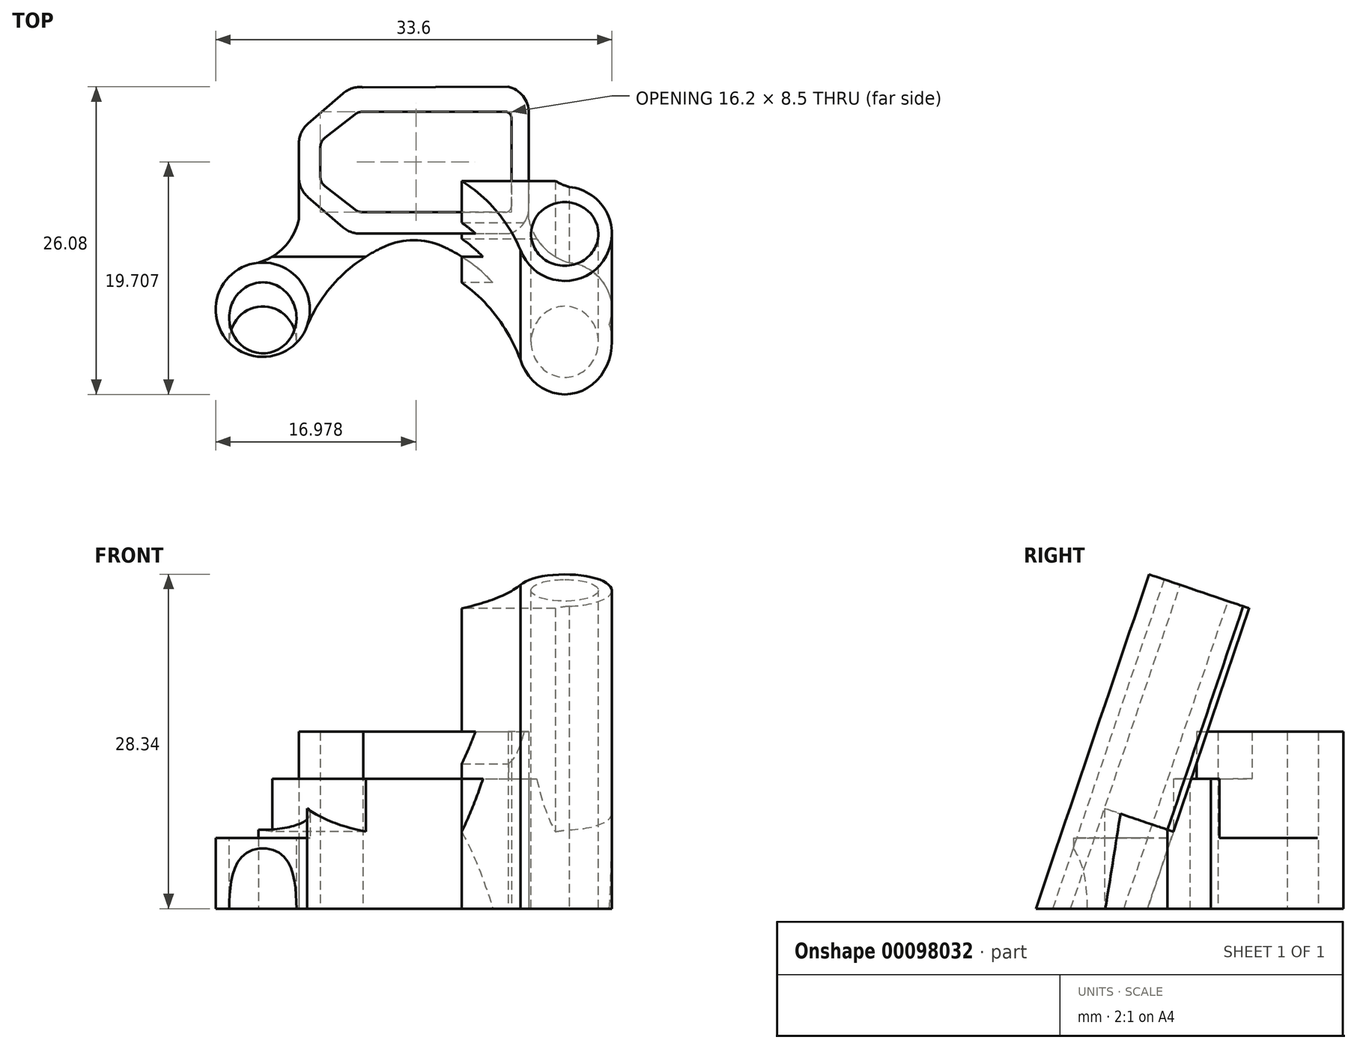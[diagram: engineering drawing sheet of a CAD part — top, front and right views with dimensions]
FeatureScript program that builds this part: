
annotation { "Feature Type Name" : "Feature", "Feature Type Description" : "" }
export const myFeature = defineFeature(function(context is Context, id is Id, definition is map)
    precondition{}
    {
        {
            var Q0;
            Q0=qCreatedBy(makeId("Top.planeOp"),FACE);
            var sketch = newSketch(context, id + "F0", { "sketchPlane" : qUnion([Q0])});
            skLineSegment(sketch, "E0", {"start": v(0.28, -14.51) * mm, "end": v(13.08, -14.51) * mm, "construction": true});
            skLineSegment(sketch, "E1", {"start": v(0.28, -14.51) * mm, "end": v(0.28, -2.01) * mm, "construction": true});
            skLineSegment(sketch, "E2.0", {"start": v(-4.02, 4.34) * mm, "end": v(8.28, 4.38) * mm});
            skLineSegment(sketch, "E3.0", {"start": v(-5.73, 3.81) * mm, "end": v(-8.7, 1.24) * mm});
            skLineSegment(sketch, "E4.0", {"start": v(10.02, -6.85) * mm, "end": v(10.02, 2.19) * mm});
            skLineSegment(sketch, "E5.MirrorCS", {"start": v(-9.47, -6.85) * mm, "end": v(-9.47, -0.37) * mm});
            skArc(sketch, "E6", {"start": v(-8.7, 1.24) * mm, "mid": v(-9.25, 0.52) * mm, "end": v(-9.47, -0.37) * mm});
            skPoint(sketch, "E7.orphan", {"position": v(-9.47, 2.19) * mm});
            skPoint(sketch, "E8.orphan", {"position": v(-9.47, -9.56) * mm});
            skArc(sketch, "E9", {"start": v(-4.02, 4.34) * mm, "mid": v(-4.93, 4.26) * mm, "end": v(-5.73, 3.81) * mm});
            skArc(sketch, "E10", {"start": v(10.02, 2.19) * mm, "mid": v(9.54, 3.6) * mm, "end": v(8.28, 4.38) * mm});
            skPoint(sketch, "E11.orphan", {"position": v(10.02, -9.56) * mm});
            skPoint(sketch, "E12.visualSharp", {"position": v(-11.2, -17.76) * mm});
            skArc(sketch, "E12.filletArc", {"start": v(-11.24, -17.77) * mm, "mid": v(-11.21, -17.75) * mm, "end": v(-11.2, -17.73) * mm});
            skArc(sketch, "E13", {"start": v(9.31, -15.87) * mm, "mid": v(16.24, -16.97) * mm, "end": v(13.46, -10.53) * mm});
            skArc(sketch, "E14", {"start": v(10.02, -6.85) * mm, "mid": v(11.23, -9.17) * mm, "end": v(13.46, -10.53) * mm});
            skArc(sketch, "E15.MirrorCS", {"start": v(-8.76, -15.87) * mm, "mid": v(-15.68, -16.97) * mm, "end": v(-12.9, -10.53) * mm});
            skArc(sketch, "E16.MirrorCS", {"start": v(-9.47, -6.85) * mm, "mid": v(-10.67, -9.17) * mm, "end": v(-12.9, -10.53) * mm});
            skPoint(sketch, "E17.orphan", {"position": v(2.83, -12.51) * mm});
            skPoint(sketch, "E18.0.start.orphan", {"position": v(-2.27, -12.51) * mm});
            skPoint(sketch, "E19.orphan", {"position": v(-1.11, -9.3) * mm});
            skPoint(sketch, "E20.center.orphan", {"position": v(0.28, -12.51) * mm});
            skPoint(sketch, "E20.start.orphan", {"position": v(1.67, -9.3) * mm});
            skCircle(sketch, "E21", {"center": v(0.28, -14.51) * mm, "radius": 5.89 * mm});
            skArc(sketch, "E22", {"start": v(-1.95, -9.06) * mm, "mid": v(-6.02, -11.8) * mm, "end": v(-8.76, -15.87) * mm});
            skArc(sketch, "E23.MirrorCS", {"start": v(2.5, -9.06) * mm, "mid": v(6.58, -11.8) * mm, "end": v(9.31, -15.87) * mm});
            skSolve(sketch);
        }
        {
            var Q0;
            Q0=makeQuery(id+"F0.imprint","IMPRINT",FACE,{"disambiguationData":[TD([[makeQuery(id+"F0.imprint","IMPRINT",EDGE,{"derivedFrom":sQuery(id+"F0.wireOp",EDGE,"d4629911-5982-4b6f-971a-48b49fc914d7")}),1.0]])]});
            var Q1;
            Q1=makeQuery(id+"F0.imprint","IMPRINT",FACE,{"disambiguationData":[TD([[makeQuery(id+"F0.imprint","IMPRINT",EDGE,{"derivedFrom":sQuery(id+"F0.wireOp",EDGE,"0au38lyi-hCIC-q0mX-iSc1-wrUDnvVJG4AV")}),-1.0]])]});
            var Q2;
            Q2=makeQuery(id+"F0.imprint","IMPRINT",FACE,{"disambiguationData":[TD([[makeQuery(id+"F0.imprint","IMPRINT",EDGE,{"derivedFrom":sQuery(id+"F0.wireOp",EDGE,"E2.0")}),-1.0]])]});
            extrude(context, id + "F1", {"entities" : qUnion([Q0, Q1, Q2]), "depth" : 6 * mm});
        }
        {
            var Q0;
            Q0=qCreatedBy(makeId("Top.planeOp"),FACE);
            var sketch = newSketch(context, id + "F2", { "sketchPlane" : qUnion([Q0])});
            skPoint(sketch, "E24.endSnap0", {"position": v(10, -2.09) * mm});
            skLineSegment(sketch, "E25", {"start": v(0.56, -2) * mm, "end": v(0.56, 2.26) * mm, "construction": true});
            skLineSegment(sketch, "E26", {"start": v(0.56, -2) * mm, "end": v(8.56, -2) * mm, "construction": true});
            skLineSegment(sketch, "E27", {"start": v(0.56, -2) * mm, "end": v(-7.64, -2) * mm, "construction": true});
            skLineSegment(sketch, "E28", {"start": v(8.56, 1.76) * mm, "end": v(8.56, -2) * mm});
            skLineSegment(sketch, "E29", {"start": v(8.06, 2.26) * mm, "end": v(-4.1, 2.26) * mm});
            skLineSegment(sketch, "E30", {"start": v(-7.64, -2) * mm, "end": v(-7.64, -0.73) * mm});
            skLineSegment(sketch, "E31", {"start": v(-7.26, 0.06) * mm, "end": v(-4.71, 2.04) * mm});
            skLineSegment(sketch, "E32.MirrorCS", {"start": v(8.06, -6.24) * mm, "end": v(-4.1, -6.24) * mm});
            skLineSegment(sketch, "E33.MirrorCS", {"start": v(-7.26, -4.04) * mm, "end": v(-4.71, -6.03) * mm});
            skLineSegment(sketch, "E34.MirrorCS", {"start": v(8.56, -5.74) * mm, "end": v(8.56, -2) * mm});
            skLineSegment(sketch, "E35.MirrorCS", {"start": v(-7.64, -2) * mm, "end": v(-7.64, -3.26) * mm});
            skPoint(sketch, "E36.visualSharp", {"position": v(-4.44, 2.26) * mm});
            skArc(sketch, "E36.filletArc", {"start": v(-4.1, 2.26) * mm, "mid": v(-4.42, 2.2) * mm, "end": v(-4.71, 2.04) * mm});
            skPoint(sketch, "E37.visualSharp", {"position": v(-4.44, -6.24) * mm});
            skArc(sketch, "E37.filletArc", {"start": v(-4.71, -6.03) * mm, "mid": v(-4.42, -6.19) * mm, "end": v(-4.1, -6.24) * mm});
            skPoint(sketch, "E38.visualSharp", {"position": v(8.56, -6.24) * mm});
            skArc(sketch, "E38.filletArc", {"start": v(8.06, -6.24) * mm, "mid": v(8.41, -6.1) * mm, "end": v(8.56, -5.74) * mm});
            skPoint(sketch, "E39.visualSharp", {"position": v(8.56, 2.26) * mm});
            skArc(sketch, "E39.filletArc", {"start": v(8.56, 1.76) * mm, "mid": v(8.41, 2.11) * mm, "end": v(8.06, 2.26) * mm});
            skPoint(sketch, "E40.visualSharp", {"position": v(-7.64, -0.24) * mm});
            skArc(sketch, "E40.filletArc", {"start": v(-7.26, 0.06) * mm, "mid": v(-7.54, -0.3) * mm, "end": v(-7.64, -0.73) * mm});
            skPoint(sketch, "E41.visualSharp", {"position": v(-7.64, -3.74) * mm});
            skArc(sketch, "E41.filletArc", {"start": v(-7.64, -3.26) * mm, "mid": v(-7.54, -3.7) * mm, "end": v(-7.26, -4.04) * mm});
            skSolve(sketch);
        }
        {
            var Q0;
            Q0=makeQuery(id+"F1.opExtrude","CAP_FACE",FACE,{"disambiguationData":[OSD([sQuery(id+"F0.wireOp",EDGE,"d4629911-5982-4b6f-971a-48b49fc914d7"),sQuery(id+"F0.wireOp",EDGE,"ImPutx2W-QFbD-qxW8-i78L-FSTvowUHSBiY"),sQuery(id+"F0.wireOp",EDGE,"0au38lyi-hCIC-q0mX-iSc1-wrUDnvVJG4AV"),sQuery(id+"F0.wireOp",EDGE,"5GcbmP7J-5BBl-LmHP-MmH2-9AxPp5P0YJ5J"),sQuery(id+"F0.wireOp",EDGE,"0c2c2197-edc9-4d1a-bcad-389273000be50.MirrorC"),sQuery(id+"F0.wireOp",EDGE,"64c9b68c-6c8e-4ed3-918d-72e7e8f609220.MirrorC"),sQuery(id+"F0.wireOp",EDGE,"E2.0"),sQuery(id+"F0.wireOp",EDGE,"E3.0"),sQuery(id+"F0.wireOp",EDGE,"E4.0"),sQuery(id+"F0.wireOp",EDGE,"E5.MirrorCS"),sQuery(id+"F0.wireOp",EDGE,"E18.0"),sQuery(id+"F0.wireOp",EDGE,"JLQODHdW-MHJ0-otSJ-f0Qb-LNSRgQ6JGbO4"),sQuery(id+"F0.wireOp",EDGE,"E6"),sQuery(id+"F0.wireOp",EDGE,"E9"),sQuery(id+"F0.wireOp",EDGE,"E10"),sQuery(id+"F0.wireOp",EDGE,"d3e15ed9-6342-4c84-aa85-bc2d0c4d76830.MirrorCS"),sQuery(id+"F0.wireOp",EDGE,"E12.filletArc"),sQuery(id+"F0.wireOp",EDGE,"DGcCSlXd-i68P-Idzq-AatA-I40wMqZVzdve"),sQuery(id+"F0.wireOp",EDGE,"O1gaBR9k-BKMN-OLy6-3FAo-aSd6Bou1lmTt"),sQuery(id+"F0.wireOp",EDGE,"ptTCF1s4-ZXo4-ReFN-VLr2-CB4CUV85mEja"),sQuery(id+"F0.wireOp",EDGE,"zlLHKiyM-WCp0-oP85-up2D-3OBM3i7OTVPH"),sQuery(id+"F0.wireOp",EDGE,"H9nJKIs5-YcsU-499D-CcEw-D9t5R8ZXcTsI"),sQuery(id+"F0.wireOp",EDGE,"d137af1c-2e07-4a16-8324-2da871225d6b0.MirrorCS"),sQuery(id+"F0.wireOp",EDGE,"a3cbc734-e190-4853-8382-23770ceede0c0.MirrorCS"),sQuery(id+"F0.wireOp",EDGE,"11e9df6b-5368-4821-beaa-32eefdf8cf520.MirrorCS"),sQuery(id+"F0.wireOp",EDGE,"386b19c8-247a-42be-beb1-9e45e31ef6ce0.MirrorCS"),sQuery(id+"F0.wireOp",EDGE,"cymLgAyk-GmRh-qVGK-mBnH-K3FJyQDvy6Oq")])],"isStart":false});
            var sketch = newSketch(context, id + "F3", { "sketchPlane" : qUnion([Q0])});
            skLineSegment(sketch, "E42", {"start": v(-7.3, -1.87) * mm, "end": v(8.25, -1.84) * mm, "construction": true});
            skLineSegment(sketch, "E43", {"start": v(-4.02, 4.34) * mm, "end": v(8.28, 4.38) * mm});
            skLineSegment(sketch, "E44", {"start": v(-5.73, 3.81) * mm, "end": v(-8.7, 1.24) * mm});
            skLineSegment(sketch, "E45", {"start": v(10.02, 2.19) * mm, "end": v(10.04, -5.87) * mm});
            skArc(sketch, "E46", {"start": v(-4.02, 4.34) * mm, "mid": v(-4.93, 4.26) * mm, "end": v(-5.73, 3.81) * mm});
            skArc(sketch, "E47", {"start": v(10.02, 2.19) * mm, "mid": v(9.54, 3.6) * mm, "end": v(8.28, 4.38) * mm});
            skArc(sketch, "E48", {"start": v(-8.7, 1.24) * mm, "mid": v(-9.25, 0.52) * mm, "end": v(-9.47, -0.37) * mm});
            skLineSegment(sketch, "E49.MirrorCS", {"start": v(-5.71, -7.54) * mm, "end": v(-8.7, -4.97) * mm});
            skArc(sketch, "E50.MirrorCS", {"start": v(-8.7, -4.97) * mm, "mid": v(-9.25, -4.25) * mm, "end": v(-9.46, -3.37) * mm});
            skLineSegment(sketch, "E51.MirrorCS", {"start": v(-4, -8.06) * mm, "end": v(8.3, -8.07) * mm});
            skArc(sketch, "E52.MirrorCS", {"start": v(10.04, -5.87) * mm, "mid": v(9.55, -7.27) * mm, "end": v(8.3, -8.07) * mm});
            skArc(sketch, "E53.MirrorCS", {"start": v(-4, -8.06) * mm, "mid": v(-4.91, -7.98) * mm, "end": v(-5.71, -7.54) * mm});
            skLineSegment(sketch, "E54", {"start": v(-9.46, -3.37) * mm, "end": v(-9.47, -0.37) * mm});
            skSolve(sketch);
        }
        {
            var Q0;
            Q0 = qSketchRegion(id + "F3", true);
            extrude(context, id + "F4", {"entities" : qUnion([Q0]), "operationType" : NewBodyOperationType.ADD, "depth" : 9 * mm});
        }
        {
            var Q0;
            Q0 = qSketchRegion(id + "F2", true);
            extrude(context, id + "F5", {"entities" : qUnion([Q0]), "operationType" : NewBodyOperationType.REMOVE, "depth" : 25 * mm});
        }
        {
            var Q0;
            Q0=makeQuery(id+"F1.opExtrude","CAP_FACE",FACE,{"disambiguationData":[OSD([sQuery(id+"F0.wireOp",EDGE,"0au38lyi-hCIC-q0mX-iSc1-wrUDnvVJG4AV"),sQuery(id+"F0.wireOp",EDGE,"0c2c2197-edc9-4d1a-bcad-389273000be50.MirrorC"),sQuery(id+"F0.wireOp",EDGE,"E2.0"),sQuery(id+"F0.wireOp",EDGE,"E3.0"),sQuery(id+"F0.wireOp",EDGE,"E4.0"),sQuery(id+"F0.wireOp",EDGE,"E5.MirrorCS"),sQuery(id+"F0.wireOp",EDGE,"E6"),sQuery(id+"F0.wireOp",EDGE,"E9"),sQuery(id+"F0.wireOp",EDGE,"E10"),sQuery(id+"F0.wireOp",EDGE,"E13"),sQuery(id+"F0.wireOp",EDGE,"E14"),sQuery(id+"F0.wireOp",EDGE,"E15.MirrorCS"),sQuery(id+"F0.wireOp",EDGE,"E16.MirrorCS"),sQuery(id+"F0.wireOp",EDGE,"E21"),sQuery(id+"F0.wireOp",EDGE,"E22"),sQuery(id+"F0.wireOp",EDGE,"E23.MirrorCS")])],"isStart":false});
            var sketch = newSketch(context, id + "F6", { "sketchPlane" : qUnion([Q0])});
            skCircle(sketch, "E55", {"center": v(13.08, -14.51) * mm, "radius": 4 * mm});
            skCircle(sketch, "E56", {"center": v(-12.52, -14.51) * mm, "radius": 4 * mm});
            skSolve(sketch);
        }
        {
            var Q0;
            Q0=makeQuery(id+"F6.imprint","IMPRINT",FACE,{"disambiguationData":[TD([[makeQuery(id+"F6.imprint","IMPRINT",EDGE,{"derivedFrom":makeQuery(id+"F1.opExtrude","CAP_EDGE",EDGE,{"disambiguationData":[OSD([sQuery(id+"F0.wireOp",EDGE,"0au38lyi-hCIC-q0mX-iSc1-wrUDnvVJG4AV")])],"isStart":false})}),-1.0]])]});
            var Q1;
            {var subQ0=sQuery(id+"F6.wireOp",EDGE,"E56");Q1=makeQuery(id+"F6.imprint","IMPRINT",FACE,{"disambiguationData":[TD([[makeQuery(id+"F6.imprint","IMPRINT",EDGE,{"disambiguationData":[OD(0.0)],"derivedFrom":subQ0}),-1.0]])]});}
            var Q2;
            {var subQ0=sQuery(id+"F6.wireOp",EDGE,"E55");var subQ1=makeQuery(id+"F6.imprint","INTERSECT",VERTEX,{"derivedFrom":[makeQuery(id+"F1.opExtrude","CAP_EDGE",EDGE,{"disambiguationData":[OSD([sQuery(id+"F0.wireOp",EDGE,"E23.MirrorCS")])],"isStart":false}),subQ0]});Q2=makeQuery(id+"F6.imprint","IMPRINT",FACE,{"disambiguationData":[TD([[makeQuery(id+"F6.imprint","IMPRINT",EDGE,{"disambiguationData":[TD([[subQ1,-1.0]])],"derivedFrom":subQ0}),1.0]])]});}
            extrude(context, id + "F7", {"entities" : qUnion([Q0, Q1, Q2]), "operationType" : NewBodyOperationType.ADD, "depth" : 5 * mm});
        }
        {
            var Q0;
            Q0=qCreatedBy(makeId("Right.planeOp"),FACE);
            cPlane(context, id + "F8", {"entities" : qUnion([Q0]), "cplaneType" : CPlaneType.OFFSET, "offset" : 16.52 * mm, "oppositeDirection" : true, "width" : 150 * mm, "height" : 150 * mm});
        }
        {
            var Q0;
            Q0=qCreatedBy(id+"F8.planeOp",FACE);
            var sketch = newSketch(context, id + "F9", { "sketchPlane" : qUnion([Q0])});
            skLineSegment(sketch, "E57", {"start": v(-10.02, 6.52) * mm, "end": v(-20.57, 10.1) * mm});
            skLineSegment(sketch, "E58", {"start": v(-20.57, 10.1) * mm, "end": v(-20.57, 12.28) * mm});
            skLineSegment(sketch, "E59", {"start": v(-20.57, 12.28) * mm, "end": v(-10.02, 12.28) * mm});
            skLineSegment(sketch, "E60", {"start": v(-10.02, 12.28) * mm, "end": v(-10.02, 6.52) * mm});
            skSolve(sketch);
        }
        {
            var Q0;
            Q0=makeQuery(id+"F9.imprint","IMPRINT",FACE,{"disambiguationData":[TD([[makeQuery(id+"F9.imprint","IMPRINT",EDGE,{"derivedFrom":sQuery(id+"F9.wireOp",EDGE,"E57")}),-1.0]])]});
            extrude(context, id + "F10", {"entities" : qUnion([Q0]), "operationType" : NewBodyOperationType.REMOVE, "depth" : 100 * mm});
        }
        {
            var Q0;
            Q0=makeQuery(id+"F10.boolean.opBoolean","COPY",FACE,{"disambiguationData":[TD([makeQuery(id+"F1.opExtrude","SWEPT_FACE",FACE,{"disambiguationData":[OSD([sQuery(id+"F0.wireOp",EDGE,"E13")])]})])],"derivedFrom":makeQuery(id+"F10.opExtrude","SWEPT_FACE",FACE,{"disambiguationData":[OSD([sQuery(id+"F9.wireOp",EDGE,"E57")])]})});
            var Q1;
            Q1=makeQuery(id+"F10.boolean.opBoolean","COPY",FACE,{"disambiguationData":[TD([makeQuery(id+"F1.opExtrude","SWEPT_FACE",FACE,{"disambiguationData":[OSD([sQuery(id+"F0.wireOp",EDGE,"E15.MirrorCS")])]})])],"derivedFrom":makeQuery(id+"F10.opExtrude","SWEPT_FACE",FACE,{"disambiguationData":[OSD([sQuery(id+"F9.wireOp",EDGE,"E57")])]})});
            extrude(context, id + "F11", {"entities" : qUnion([Q0, Q1]), "operationType" : NewBodyOperationType.ADD, "oppositeDirection" : true, "depth" : 10 * mm});
        }
        {
            var Q0;
            Q0=makeQuery(id+"F10.boolean.opBoolean","COPY",FACE,{"disambiguationData":[TD([makeQuery(id+"F1.opExtrude","SWEPT_FACE",FACE,{"disambiguationData":[OSD([sQuery(id+"F0.wireOp",EDGE,"E13")])]})])],"derivedFrom":makeQuery(id+"F10.opExtrude","SWEPT_FACE",FACE,{"disambiguationData":[OSD([sQuery(id+"F9.wireOp",EDGE,"E57")])]})});
            var Q1;
            Q1=makeQuery(id+"F10.boolean.opBoolean","COPY",FACE,{"disambiguationData":[TD([makeQuery(id+"F1.opExtrude","SWEPT_FACE",FACE,{"disambiguationData":[OSD([sQuery(id+"F0.wireOp",EDGE,"E15.MirrorCS")])]})])],"derivedFrom":makeQuery(id+"F10.opExtrude","SWEPT_FACE",FACE,{"disambiguationData":[OSD([sQuery(id+"F9.wireOp",EDGE,"E57")])]})});
            extrude(context, id + "F12", {"entities" : qUnion([Q0, Q1]), "operationType" : NewBodyOperationType.ADD, "depth" : 20 * mm});
        }
        {
            var Q0;
            Q0=makeQuery(id+"F11.opExtrude","CAP_FACE",FACE,{"disambiguationData":[OSD([sQuery(id+"F9.wireOp",EDGE,"E57")])],"isStart":false});
            var Q1;
            Q1=makeQuery(id+"F1.opExtrude","CAP_FACE",FACE,{"disambiguationData":[OSD([sQuery(id+"F0.wireOp",EDGE,"E2.0"),sQuery(id+"F0.wireOp",EDGE,"E3.0"),sQuery(id+"F0.wireOp",EDGE,"E4.0"),sQuery(id+"F0.wireOp",EDGE,"E5.MirrorCS"),sQuery(id+"F0.wireOp",EDGE,"E6"),sQuery(id+"F0.wireOp",EDGE,"E9"),sQuery(id+"F0.wireOp",EDGE,"E10"),sQuery(id+"F0.wireOp",EDGE,"E13"),sQuery(id+"F0.wireOp",EDGE,"E14"),sQuery(id+"F0.wireOp",EDGE,"E15.MirrorCS"),sQuery(id+"F0.wireOp",EDGE,"E16.MirrorCS"),sQuery(id+"F0.wireOp",EDGE,"E21"),sQuery(id+"F0.wireOp",EDGE,"E22"),sQuery(id+"F0.wireOp",EDGE,"E23.MirrorCS")])],"isStart":true});
            extrude(context, id + "F13", {"entities" : qUnion([Q0]), "operationType" : NewBodyOperationType.REMOVE, "endBound" : BoundingType.UP_TO_SURFACE, "oppositeDirection" : true, "endBoundEntityFace" : qUnion([Q1]), "depth" : 25 * mm});
        }
        {
            var Q0;
            {var subQ0=sQuery(id+"F9.wireOp",EDGE,"E57");Q0=makeQuery(id+"F12.opExtrude","CAP_FACE",FACE,{"disambiguationData":[OSD([subQ0]),TDD([makeQuery(id+"F10.boolean.opBoolean","COPY",FACE,{"disambiguationData":[TD([makeQuery(id+"F1.opExtrude","SWEPT_FACE",FACE,{"disambiguationData":[OSD([sQuery(id+"F0.wireOp",EDGE,"E15.MirrorCS")])]})])],"derivedFrom":makeQuery(id+"F10.opExtrude","SWEPT_FACE",FACE,{"disambiguationData":[OSD([subQ0])]})})])],"isStart":false});}
            var sketch = newSketch(context, id + "F14", { "sketchPlane" : qUnion([Q0])});
            skCircle(sketch, "E61", {"center": v(-12.52, -16.33) * mm, "radius": 2.85 * mm});
            skSolve(sketch);
        }
        {
            var Q0;
            Q0=makeQuery(id+"F14.imprint","IMPRINT",FACE,{"disambiguationData":[TD([[makeQuery(id+"F14.imprint","IMPRINT",EDGE,{"derivedFrom":sQuery(id+"F14.wireOp",EDGE,"E61")}),1.0]])]});
            extrude(context, id + "F15", {"entities" : qUnion([Q0]), "operationType" : NewBodyOperationType.REMOVE, "oppositeDirection" : true, "depth" : 35 * mm});
        }
        {
            var Q0;
            {var subQ0=sQuery(id+"F9.wireOp",EDGE,"E57");Q0=makeQuery(id+"F12.opExtrude","CAP_FACE",FACE,{"disambiguationData":[OSD([subQ0]),TDD([makeQuery(id+"F10.boolean.opBoolean","COPY",FACE,{"disambiguationData":[TD([makeQuery(id+"F1.opExtrude","SWEPT_FACE",FACE,{"disambiguationData":[OSD([sQuery(id+"F0.wireOp",EDGE,"E13")])]})])],"derivedFrom":makeQuery(id+"F10.opExtrude","SWEPT_FACE",FACE,{"disambiguationData":[OSD([subQ0])]})})])],"isStart":false});}
            var sketch = newSketch(context, id + "F16", { "sketchPlane" : qUnion([Q0])});
            skCircle(sketch, "E62", {"center": v(13.08, -16.33) * mm, "radius": 2.85 * mm});
            skSolve(sketch);
        }
        {
            var Q0;
            Q0 = qSketchRegion(id + "F16", true);
            extrude(context, id + "F17", {"entities" : qUnion([Q0]), "operationType" : NewBodyOperationType.REMOVE, "oppositeDirection" : true, "depth" : 35 * mm});
        }
    });
